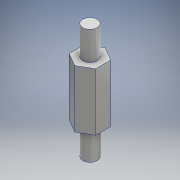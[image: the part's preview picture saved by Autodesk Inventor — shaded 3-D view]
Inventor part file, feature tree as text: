
AUTODESK INVENTOR PART (.ipt)
format: ipt  version: 2016 (Build 200138000, 138)  size: 107,008 bytes
history: native  units: mm
features: extrude x3, sketch x2, other x1
ambient origin geometry x8: Origin, YZ Plane, XZ Plane, XY Plane, X Axis, Y Axis, Z Axis, Center Point
bodies: Body1 (feature_tree)
feature tree (6):
  other  "ソリッド1"
  sketch  "スケッチ1"
  extrude  "押し出し1"  Depth=5.5mm
  extrude  "押し出し2"  Depth=3.0mm
  extrude  "押し出し3"  Depth=12.0mm TaperAngle=0.0deg
  sketch  "スケッチ2"
